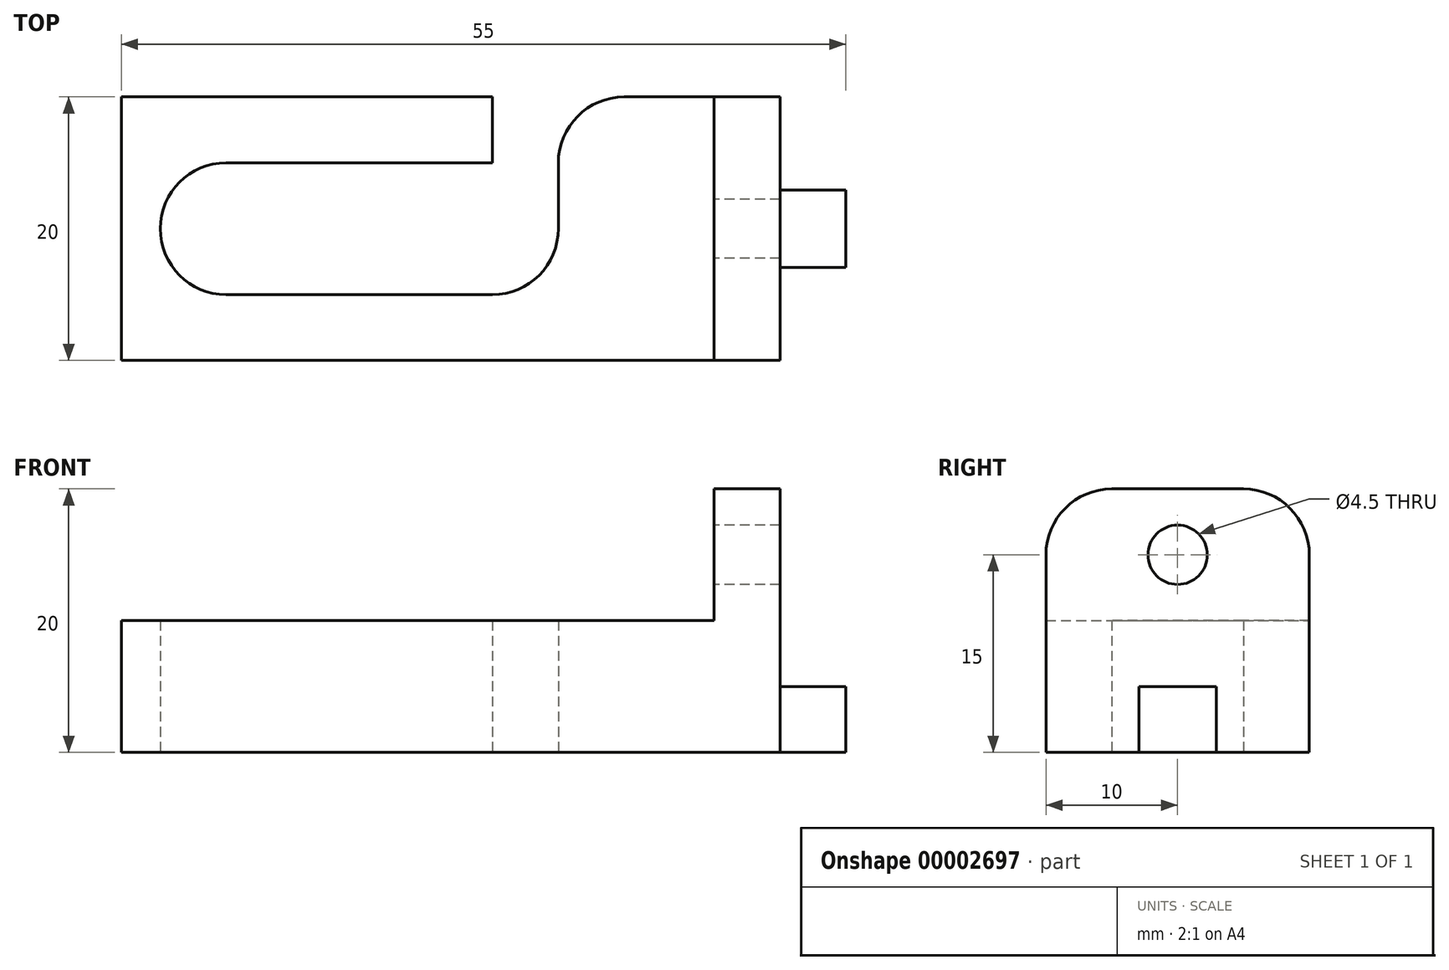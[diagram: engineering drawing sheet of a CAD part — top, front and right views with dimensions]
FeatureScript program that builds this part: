
annotation { "Feature Type Name" : "Feature", "Feature Type Description" : "" }
export const myFeature = defineFeature(function(context is Context, id is Id, definition is map)
    precondition{}
    {
        {
            var Q0;
            Q0=qCreatedBy(makeId("Top.planeOp"),FACE);
            var sketch = newSketch(context, id + "F0", { "sketchPlane" : qUnion([Q0])});
            skLineSegment(sketch, "E0.bottom", {"start": v(-11.77, 0) * mm, "end": v(38.23, 0) * mm});
            skLineSegment(sketch, "E0.top", {"start": v(-11.77, 20) * mm, "end": v(38.23, 20) * mm});
            skLineSegment(sketch, "E0.left", {"start": v(-11.77, 0) * mm, "end": v(-11.77, 20) * mm});
            skLineSegment(sketch, "E0.right", {"start": v(38.23, 0) * mm, "end": v(38.23, 20) * mm});
            skLineSegment(sketch, "E1.bottom", {"start": v(-8.83, 15) * mm, "end": v(21.4, 15) * mm});
            skLineSegment(sketch, "E1.top", {"start": v(-8.83, 5) * mm, "end": v(21.4, 5) * mm});
            skLineSegment(sketch, "E1.left", {"start": v(-8.83, 15) * mm, "end": v(-8.83, 5) * mm});
            skLineSegment(sketch, "E1.right", {"start": v(21.4, 15) * mm, "end": v(21.4, 5) * mm});
            skLineSegment(sketch, "E2", {"start": v(5.68, 0) * mm, "end": v(5.68, 5) * mm});
            skLineSegment(sketch, "E3", {"start": v(5.68, 15) * mm, "end": v(5.68, 20) * mm});
            skLineSegment(sketch, "E4.bottom", {"start": v(21.4, 15) * mm, "end": v(16.4, 15) * mm});
            skLineSegment(sketch, "E4.top", {"start": v(21.4, 20) * mm, "end": v(16.4, 20) * mm});
            skLineSegment(sketch, "E4.left", {"start": v(21.4, 15) * mm, "end": v(21.4, 20) * mm});
            skLineSegment(sketch, "E4.right", {"start": v(16.4, 15) * mm, "end": v(16.4, 20) * mm});
            skLineSegment(sketch, "E5.bottom", {"start": v(38.23, 12.95) * mm, "end": v(43.23, 12.95) * mm});
            skLineSegment(sketch, "E5.top", {"start": v(38.23, 7.05) * mm, "end": v(43.23, 7.05) * mm});
            skLineSegment(sketch, "E5.left", {"start": v(38.23, 12.95) * mm, "end": v(38.23, 7.05) * mm});
            skLineSegment(sketch, "E5.right", {"start": v(43.23, 12.95) * mm, "end": v(43.23, 7.05) * mm});
            skPoint(sketch, "E6", {"position": v(21.4, 10) * mm});
            skPoint(sketch, "E7", {"position": v(43.23, 10) * mm});
            skSolve(sketch);
        }
        {
            var Q0;
            {var subQ3=sQuery(id+"F0.wireOp",EDGE,"E0.left");Q0=makeQuery(id+"F0.imprint","IMPRINT",FACE,{"disambiguationData":[TD([[makeQuery(id+"F0.imprint","IMPRINT",EDGE,{"derivedFrom":subQ3}),-1.0]])]});}
            var Q1;
            {var subQ3=sQuery(id+"F0.wireOp",EDGE,"E0.right");Q1=makeQuery(id+"F0.imprint","IMPRINT",FACE,{"disambiguationData":[TD([[makeQuery(id+"F0.imprint","IMPRINT",EDGE,{"derivedFrom":subQ3}),1.0]])]});}
            var Q2;
            {var subQ0=sQuery(id+"F0.wireOp",EDGE,"E3");Q2=makeQuery(id+"F0.imprint","IMPRINT",FACE,{"disambiguationData":[TD([[makeQuery(id+"F0.imprint","IMPRINT",EDGE,{"derivedFrom":subQ0}),-1.0]])]});}
            extrude(context, id + "F1", {"entities" : qUnion([Q0, Q1, Q2]), "depth" : 10 * mm});
        }
        {
            var Q0;
            Q0=makeQuery(id+"F0.imprint","IMPRINT",FACE,{"disambiguationData":[TD([[makeQuery(id+"F0.imprint","IMPRINT",EDGE,{"derivedFrom":sQuery(id+"F0.wireOp",EDGE,"E5.bottom")}),-1.0]])]});
            extrude(context, id + "F2", {"entities" : qUnion([Q0]), "operationType" : NewBodyOperationType.ADD, "depth" : 5 * mm});
        }
        {
            var Q0;
            Q0=makeQuery(id+"F1.opExtrude","CAP_FACE",FACE,{"disambiguationData":[OSD([sQuery(id+"F0.wireOp",EDGE,"E0.bottom"),sQuery(id+"F0.wireOp",EDGE,"E0.top"),sQuery(id+"F0.wireOp",EDGE,"E0.left"),sQuery(id+"F0.wireOp",EDGE,"E0.right"),sQuery(id+"F0.wireOp",EDGE,"E1.bottom"),sQuery(id+"F0.wireOp",EDGE,"E1.top"),sQuery(id+"F0.wireOp",EDGE,"E1.left"),sQuery(id+"F0.wireOp",EDGE,"E1.right"),sQuery(id+"F0.wireOp",EDGE,"E4.left"),sQuery(id+"F0.wireOp",EDGE,"E4.right"),sQuery(id+"F0.wireOp",EDGE,"E5.left")])],"isStart":false});
            var sketch = newSketch(context, id + "F3", { "sketchPlane" : qUnion([Q0])});
            skLineSegment(sketch, "E8.bottom", {"start": v(38.23, 20) * mm, "end": v(33.23, 20) * mm});
            skLineSegment(sketch, "E8.top", {"start": v(38.23, 0) * mm, "end": v(33.23, 0) * mm});
            skLineSegment(sketch, "E8.left", {"start": v(38.23, 20) * mm, "end": v(38.23, 0) * mm});
            skLineSegment(sketch, "E8.right", {"start": v(33.23, 20) * mm, "end": v(33.23, 0) * mm});
            skSolve(sketch);
        }
        {
            var Q0;
            Q0 = qSketchRegion(id + "F3", true);
            extrude(context, id + "F4", {"entities" : qUnion([Q0]), "operationType" : NewBodyOperationType.ADD, "depth" : 10 * mm});
        }
        {
            var Q0;
            Q0=makeQuery(id+"F4.opExtrude","SWEPT_FACE",FACE,{"disambiguationData":[OSD([sQuery(id+"F3.wireOp",EDGE,"E8.right")])]});
            var sketch = newSketch(context, id + "F5", { "sketchPlane" : qUnion([Q0])});
            skCircle(sketch, "E9", {"center": v(-10, 15) * mm, "radius": 2.25 * mm});
            skPoint(sketch, "E10", {"position": v(-10, 20) * mm});
            skPoint(sketch, "E11", {"position": v(-20, 15) * mm});
            skSolve(sketch);
        }
        {
            var Q0;
            Q0 = qSketchRegion(id + "F5", true);
            extrude(context, id + "F6", {"entities" : qUnion([Q0]), "operationType" : NewBodyOperationType.REMOVE, "oppositeDirection" : true, "depth" : 25 * mm});
        }
        {
            var Q0;
            Q0=makeQuery(id+"F4.opExtrude","CAP_EDGE",EDGE,{"disambiguationData":[OSD([sQuery(id+"F3.wireOp",EDGE,"E8.top")])],"isStart":false});
            var Q1;
            Q1=makeQuery(id+"F4.opExtrude","CAP_EDGE",EDGE,{"disambiguationData":[OSD([sQuery(id+"F3.wireOp",EDGE,"E8.bottom")])],"isStart":false});
            var Q2;
            Q2=makeQuery(id+"F1.opExtrude","SWEPT_EDGE",EDGE,{"disambiguationData":[OSD([sQuery(id+"F0.wireOp",EDGE,"E1.bottom"),sQuery(id+"F0.wireOp",EDGE,"E1.left")])]});
            var Q3;
            Q3=makeQuery(id+"F1.opExtrude","SWEPT_EDGE",EDGE,{"disambiguationData":[OSD([sQuery(id+"F0.wireOp",EDGE,"E1.top"),sQuery(id+"F0.wireOp",EDGE,"E1.left")])]});
            var Q4;
            Q4=makeQuery(id+"F1.opExtrude","SWEPT_EDGE",EDGE,{"disambiguationData":[OSD([sQuery(id+"F0.wireOp",EDGE,"E1.top"),sQuery(id+"F0.wireOp",EDGE,"E1.right")])]});
            var Q5;
            Q5=makeQuery(id+"F1.opExtrude","SWEPT_EDGE",EDGE,{"disambiguationData":[OSD([sQuery(id+"F0.wireOp",EDGE,"E0.top"),sQuery(id+"F0.wireOp",EDGE,"E4.top"),sQuery(id+"F0.wireOp",EDGE,"E4.left")])]});
            fillet(context, id + "F7", {"entities" : qUnion([Q0, Q1, Q2, Q3, Q4, Q5]), "radius" : 5 * mm, "tangentPropagation" : true, "allowEdgeOverflow" : false});
        }
    });
